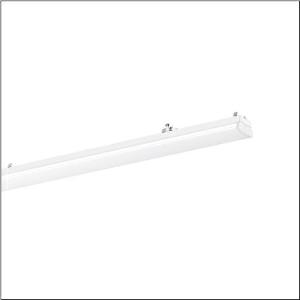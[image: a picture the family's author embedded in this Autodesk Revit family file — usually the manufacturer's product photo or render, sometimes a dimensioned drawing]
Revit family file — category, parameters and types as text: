
# Revit family: licross_r__11_recessed_opal_mo_51tl1ddv495g_cbeb
name_source: partatom
category: Lighting Fixtures
units: mm (PartAtom-declared; Revit-internal decimal feet)

## family parameters
Cut with Voids When Loaded = No
Host = Face
Light Source = No
Part Type = Normal
Room Calculation Point = No
Round Connector Dimension = Use Diameter
Shared = No

## types (1)
- --- (1 x LED, 9500 lm, 52.6 W, 4000K)
    Apparent Load = 53 VA
    CIE Flux Codes = 44 73 91 87 100
    Color Rendering = 80
    Color Temperature = 4000K
    Default Elevation = 1800 mm
    Description = Licross® 11 recessed opal MO, luminaire insert, of sheet steel, coil coated, white, length: 2.250mm, width: 76mm, height: 87mm, LED rated luminous flux: 9.500lm, light colour: 840, control gear: DALI 2, with plug, 5-pole, with phase selection, mains connection: 220..240V, AC, 50/60Hz, rated input power: 53W, halogen-free wiring, primary optical cover: cover, of PMMA, light emission: direct with ceiling illumination distribution, primary light characteristic: symmetric, protection rating (complete): IP40, insulation class (complete): insulation class I (protective earthing), certification: CE, ENEC, VDE, UKCA, protection symbol: D if used in an environment without relevant dust loads with corresponding accessories, impact resistance: IK06, permissible ambient temperature for indoor applications: -25..+40°C, corresponds to IFS (International Featured Standards) requirements for safety and quality in the food industry, reducing of maximum allowable ambient temperature of 5°C with ceiling mounting, LABS conformity tested according to VDMA 24364:2018-05, packaging unit: 1 piece
    Height = 83 mm
    Lamp = 1 x LED
    Lamp Light Flux = 9500 lm
    Lamp Power = 52.6 W
    Lamp count = 1
    Length = 2250 mm
    Luminous efficacy = 181 lm/W
    Manufacturer = Siteco
    ModVariant = No
    Model = 51TL1DDV495G
    Mounting Place = Ceiling
    Mounting Type = Pendant
    Number of Poles = 1
    OnlyDefault = Yes
    Power Factor = 1
    Product Name = Licross® 11 recessed opal MO
    Product group = luminaire insert
    ProductGroupID = 901
    Protection Class = Protection class I
    Protection Degree = IP 40
    RLX_Detail_Level = 1
    RLX_Emergency_Light_Flux = 0 lm
    RLX_Emergency_Type = 0
    RLX_Emergency_Type_DB = No
    RlxData = <blob elided: 26593 chars, md5=0b33a4a6>
    Socket = socket
    Standby Power = 0 W
    System Light Flux = 9500 lm
    System Power = 53 W
    Type Comments = factory setting: luminous flux: 100 % | dim-lin: 254 | 239 mA
    Type Image = l_1313666.jpg
    URL = http://relux.com
    VarID = @adj_045491
    Voltage = 0 V
    Weight = 0.00 kg
    Width = 76 mm

## geometry (parser evidence)
native form markers: Blend x4, Sweep x14
no freeform markers — native parametric forms only
